# Revit family: C8183
name_source: partatom
category: Specialty Equipment
units: mm (PartAtom-declared; Revit-internal decimal feet)

## family parameters
Always vertical = No
Cut with Voids When Loaded = No
Maintain Annotation Orientation = No
Part Type = Normal
Room Calculation Point = No
Round Connector Dimension = Use Diameter
Shared = No
Work Plane-Based = Yes

## types (1)
- C8183 Faucet
    Cold Water Consumption = 25 GPM
    Cold Water Flow Rate = 23 GPM
    Cold Water Inlet Flow = 25 GPM
    Cold Water Maximum Pressure = 125.00 psi
    Cold Water Minimum Pressure = 20.00 psi
    Cold Water Size = 1"
    Cold water Temerature Recommended = 40 °F
    Connector 2 Description = Cold Water Inlet
    Default Elevation = 48"
    Description = Hand Sink
    Faucet Material = Lead Free Brass
    Manufacturer = Krome USA Inc.
    Maximum Temperature = 140 °F
    Minimum Teperature = 40 °F
    Model = C8183
    Product Name = US Single Pantry Base Faucet - Heavy Duty - Lead Free Brass (C8183)
    URL = https://www.aluids.com
    Water Supply Radius = 1/4"

## geometry (parser evidence)
native form markers: Sweep x5
no freeform markers — native parametric forms only
